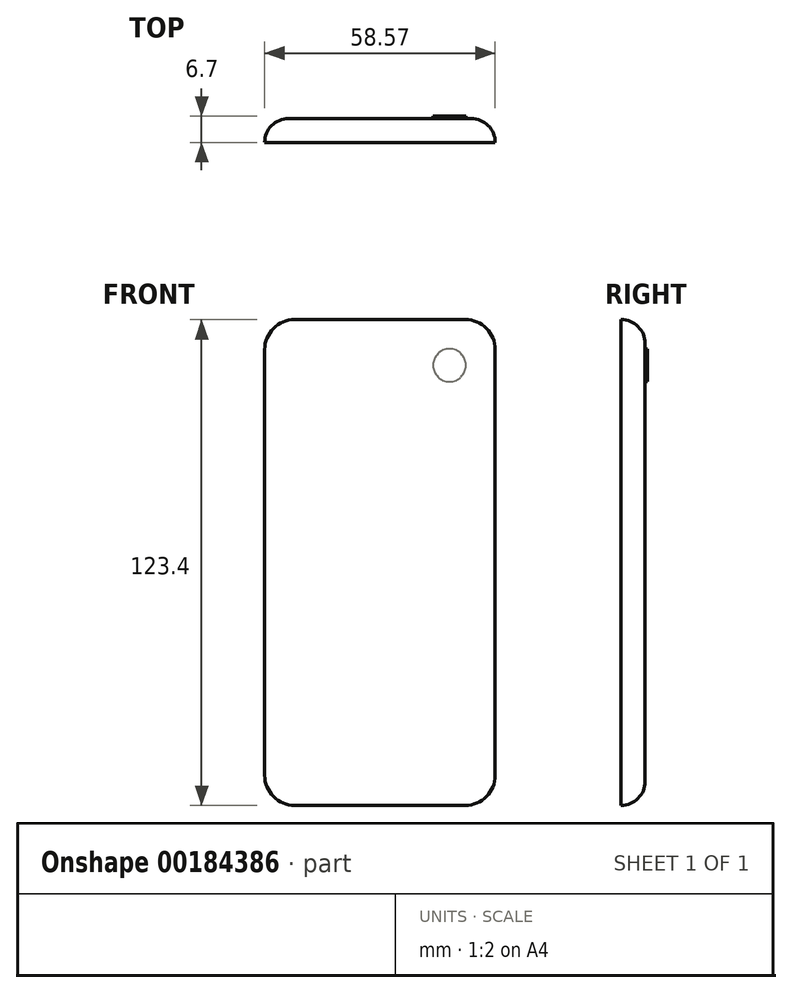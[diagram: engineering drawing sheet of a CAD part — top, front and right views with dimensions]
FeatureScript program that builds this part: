
annotation { "Feature Type Name" : "Feature", "Feature Type Description" : "" }
export const myFeature = defineFeature(function(context is Context, id is Id, definition is map)
    precondition{}
    {
        {
            var Q0;
            Q0=qCreatedBy(makeId("Front.planeOp"),FACE);
            var sketch = newSketch(context, id + "F0", { "sketchPlane" : qUnion([Q0])});
            skLineSegment(sketch, "E0.bottom", {"start": v(-34.7, 65.35) * mm, "end": v(8.62, 65.35) * mm});
            skLineSegment(sketch, "E0.top", {"start": v(-34.7, -58.05) * mm, "end": v(8.62, -58.05) * mm});
            skLineSegment(sketch, "E0.left", {"start": v(-42.33, 57.73) * mm, "end": v(-42.33, -50.43) * mm});
            skLineSegment(sketch, "E0.right", {"start": v(16.24, 57.73) * mm, "end": v(16.24, -50.43) * mm});
            skPoint(sketch, "E1.visualSharp", {"position": v(-42.33, 65.35) * mm});
            skArc(sketch, "E1.filletArc", {"start": v(-34.7, 65.35) * mm, "mid": v(-40.1, 63.12) * mm, "end": v(-42.33, 57.73) * mm});
            skPoint(sketch, "E2.visualSharp", {"position": v(16.24, 65.35) * mm});
            skArc(sketch, "E2.filletArc", {"start": v(16.24, 57.73) * mm, "mid": v(14.01, 63.12) * mm, "end": v(8.62, 65.35) * mm});
            skPoint(sketch, "E3.visualSharp", {"position": v(16.24, -58.05) * mm});
            skArc(sketch, "E3.filletArc", {"start": v(8.62, -58.05) * mm, "mid": v(14.01, -55.81) * mm, "end": v(16.24, -50.43) * mm});
            skPoint(sketch, "E4.visualSharp", {"position": v(-42.33, -58.05) * mm});
            skArc(sketch, "E4.filletArc", {"start": v(-42.33, -50.43) * mm, "mid": v(-40.1, -55.81) * mm, "end": v(-34.7, -58.05) * mm});
            skSolve(sketch);
        }
        {
            var Q0;
            Q0=qSketchRegion(id+"F0",true);
            extrude(context, id + "F1", {"entities" : qUnion([Q0]), "depth" : 6.1 * mm});
        }
        {
            var Q0;
            Q0=makeQuery(id+"F1.opExtrude","CAP_FACE",FACE,{"disambiguationData":[OSD([sQuery(id+"F0.wireOp",EDGE,"E0.bottom"),sQuery(id+"F0.wireOp",EDGE,"E0.top"),sQuery(id+"F0.wireOp",EDGE,"E0.left"),sQuery(id+"F0.wireOp",EDGE,"E0.right"),sQuery(id+"F0.wireOp",EDGE,"E1.filletArc"),sQuery(id+"F0.wireOp",EDGE,"E2.filletArc"),sQuery(id+"F0.wireOp",EDGE,"E3.filletArc"),sQuery(id+"F0.wireOp",EDGE,"E4.filletArc")])],"isStart":true});
            fillet(context, id + "F2", {"entities" : qUnion([Q0]), "radius" : 6.1 * mm, "tangentPropagation" : true, "allowEdgeOverflow" : false});
        }
        {
            var Q0;
            Q0=makeQuery(id+"F1.opExtrude","CAP_FACE",FACE,{"disambiguationData":[OSD([sQuery(id+"F0.wireOp",EDGE,"E0.bottom"),sQuery(id+"F0.wireOp",EDGE,"E0.top"),sQuery(id+"F0.wireOp",EDGE,"E0.left"),sQuery(id+"F0.wireOp",EDGE,"E0.right"),sQuery(id+"F0.wireOp",EDGE,"E1.filletArc"),sQuery(id+"F0.wireOp",EDGE,"E2.filletArc"),sQuery(id+"F0.wireOp",EDGE,"E3.filletArc"),sQuery(id+"F0.wireOp",EDGE,"E4.filletArc")])],"isStart":true});
            var sketch = newSketch(context, id + "F3", { "sketchPlane" : qUnion([Q0])});
            skCircle(sketch, "E5", {"center": v(-4.63, 53.75) * mm, "radius": 4.18 * mm});
            skSolve(sketch);
        }
        {
            var Q0;
            Q0=qSketchRegion(id+"F3",true);
            extrude(context, id + "F4", {"entities" : qUnion([Q0]), "operationType" : NewBodyOperationType.ADD, "depth" : .60 * mm});
        }
    });
